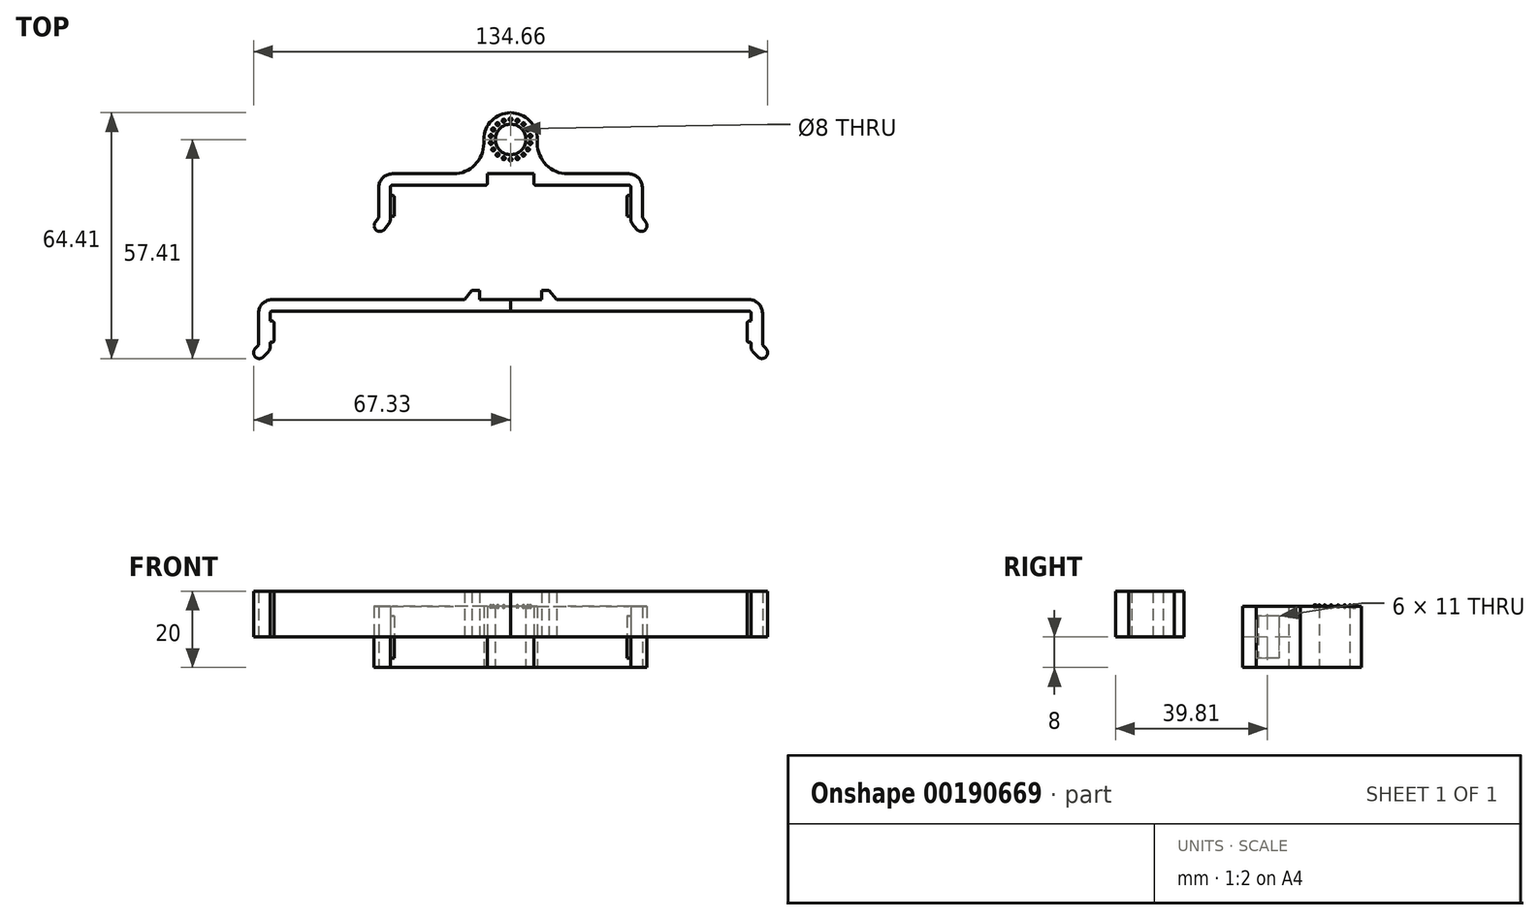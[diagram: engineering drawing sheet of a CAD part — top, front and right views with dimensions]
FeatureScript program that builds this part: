
annotation { "Feature Type Name" : "Feature", "Feature Type Description" : "" }
export const myFeature = defineFeature(function(context is Context, id is Id, definition is map)
    precondition{}
    {
        {
            var Q0;
            Q0=qCreatedBy(makeId("Top.planeOp"),FACE);
            var sketch = newSketch(context, id + "F0", { "sketchPlane" : qUnion([Q0])});
            skLineSegment(sketch, "E0", {"start": v(6.6, 0) * mm, "end": v(31, 0) * mm});
            skLineSegment(sketch, "E1", {"start": v(31.5, -0.5) * mm, "end": v(31.5, -2.6) * mm});
            skLineSegment(sketch, "E2.0", {"start": v(33.75, -2.6) * mm, "end": v(33.75, -2.6) * mm});
            skLineSegment(sketch, "E3.0", {"start": v(31, -8.1) * mm, "end": v(31, -8.1) * mm});
            skLineSegment(sketch, "E4.0", {"start": v(30.5, -3.1) * mm, "end": v(30.5, -8.1) * mm});
            skLineSegment(sketch, "E5.0", {"start": v(34.5, -0.5) * mm, "end": v(34.5, -8.55) * mm});
            skLineSegment(sketch, "E6.trimOffspring", {"start": v(31.5, -8.6) * mm, "end": v(31.5, -8.9) * mm});
            skPoint(sketch, "E7.visualSharp", {"position": v(31.5, 0) * mm});
            skArc(sketch, "E7.filletArc", {"start": v(31.5, -0.5) * mm, "mid": v(31.35, -0.15) * mm, "end": v(31, 0) * mm});
            skPoint(sketch, "E8.visualSharp", {"position": v(30.5, -8.1) * mm});
            skPoint(sketch, "E9.visualSharp", {"position": v(30.5, -2.6) * mm});
            skPoint(sketch, "E10.visualSharp", {"position": v(31.5, -8.1) * mm});
            skArc(sketch, "E10.filletArc", {"start": v(31.5, -8.6) * mm, "mid": v(31.35, -8.25) * mm, "end": v(31, -8.1) * mm});
            skPoint(sketch, "E11.visualSharp", {"position": v(31.5, -2.6) * mm});
            skPoint(sketch, "E12.visualSharp", {"position": v(34.5, 3) * mm});
            skArc(sketch, "E12.filletArc", {"start": v(34.5, -0.5) * mm, "mid": v(33.47, 1.97) * mm, "end": v(31, 3) * mm});
            skLineSegment(sketch, "E13", {"start": v(31, -2.6) * mm, "end": v(31.5, -2.6) * mm});
            skLineSegment(sketch, "E14", {"start": v(6.1, 3.1) * mm, "end": v(6.1, 0.5) * mm});
            skPoint(sketch, "E15.orphan", {"position": v(0, 0) * mm});
            skPoint(sketch, "E16.visualSharp", {"position": v(6.1, 0) * mm});
            skArc(sketch, "E16.filletArc", {"start": v(6.1, 0.5) * mm, "mid": v(6.25, 0.15) * mm, "end": v(6.6, 0) * mm});
            skPoint(sketch, "E17.visualSharp", {"position": v(9, 3) * mm});
            skLineSegment(sketch, "E18", {"start": v(0, 0) * mm, "end": v(0, 12) * mm, "construction": true});
            skArc(sketch, "E19", {"start": v(0, 8) * mm, "mid": v(4, 12) * mm, "end": v(0, 16) * mm});
            skLineSegment(sketch, "E20", {"start": v(0, 8) * mm, "end": v(0, 3) * mm});
            skLineSegment(sketch, "E21.0", {"start": v(33.25, -9.6) * mm, "end": v(34.5, -9.6) * mm, "construction": true});
            skLineSegment(sketch, "E22.0", {"start": v(33.25, -14.6) * mm, "end": v(35.5, -14.6) * mm, "construction": true});
            skLineSegment(sketch, "E23.0", {"start": v(35.5, -10.5) * mm, "end": v(35.5, -14.6) * mm, "construction": true});
            skLineSegment(sketch, "E24", {"start": v(31.94, -10.15) * mm, "end": v(33.06, -11.55) * mm});
            skLineSegment(sketch, "E25.0", {"start": v(34.5, -8.55) * mm, "end": v(35.4, -9.68) * mm});
            skLineSegment(sketch, "E26", {"start": v(31.5, -9.6) * mm, "end": v(33.84, -7.73) * mm, "construction": true});
            skLineSegment(sketch, "E27.0", {"start": v(35.17, -11.79) * mm, "end": v(35.17, -11.79) * mm});
            skPoint(sketch, "E28.visualSharp", {"position": v(34, -12.72) * mm});
            skArc(sketch, "E28.filletArc", {"start": v(33.06, -11.55) * mm, "mid": v(34.07, -12.1) * mm, "end": v(35.17, -11.79) * mm});
            skPoint(sketch, "E29.visualSharp", {"position": v(36.34, -10.85) * mm});
            skArc(sketch, "E29.filletArc", {"start": v(35.17, -11.79) * mm, "mid": v(35.72, -10.78) * mm, "end": v(35.4, -9.68) * mm});
            skPoint(sketch, "E30.visualSharp", {"position": v(31.5, -9.6) * mm});
            skArc(sketch, "E30.filletArc", {"start": v(31.5, -8.9) * mm, "mid": v(31.61, -9.56) * mm, "end": v(31.94, -10.15) * mm});
            skLineSegment(sketch, "E31.0", {"start": v(0, 3.1) * mm, "end": v(8.2, 3.1) * mm, "construction": true});
            skLineSegment(sketch, "E32", {"start": v(6.1, 3.1) * mm, "end": v(0, 3.1) * mm});
            skLineSegment(sketch, "E33.0", {"start": v(15, 3) * mm, "end": v(31, 3) * mm});
            skArc(sketch, "E34.0", {"start": v(7, 12) * mm, "mid": v(4.95, 16.95) * mm, "end": v(0, 19) * mm});
            skLineSegment(sketch, "E35.0", {"start": v(7, 0) * mm, "end": v(7, 12) * mm, "construction": true});
            skLineSegment(sketch, "E36", {"start": v(7, 11) * mm, "end": v(7, 12) * mm});
            skLineSegment(sketch, "E37", {"start": v(0, 19) * mm, "end": v(0, 16) * mm});
            skPoint(sketch, "E38.visualSharp", {"position": v(7, 3) * mm});
            skArc(sketch, "E38.filletArc", {"start": v(7, 11) * mm, "mid": v(9.34, 5.34) * mm, "end": v(15, 3) * mm});
            skLineSegment(sketch, "E39", {"start": v(30.5, -8.1) * mm, "end": v(31, -8.1) * mm});
            skArc(sketch, "E40.filletArc", {"start": v(31, -2.6) * mm, "mid": v(30.65, -2.75) * mm, "end": v(30.5, -3.1) * mm});
            skSolve(sketch);
        }
        {
            var Q0;
            Q0=makeQuery(id+"F0.imprint","IMPRINT",FACE,{"disambiguationData":[TD([[makeQuery(id+"F0.imprint","IMPRINT",EDGE,{"derivedFrom":sQuery(id+"F0.wireOp",EDGE,"E0")}),1.0]])]});
            extrude(context, id + "F1", {"entities" : qUnion([Q0]), "depth" : 5.5 * mm});
        }
        {
            var Q0;
            Q0=qCreatedBy(makeId("Top.planeOp"),FACE);
            cPlane(context, id + "F2", {"entities" : qUnion([Q0]), "cplaneType" : CPlaneType.OFFSET, "offset" : 8 * mm, "width" : 150 * mm, "height" : 150 * mm});
        }
        {
            var Q0;
            Q0=qCreatedBy(id+"F2.planeOp",FACE);
            var sketch = newSketch(context, id + "F3", { "sketchPlane" : qUnion([Q0])});
            skArc(sketch, "E41.0.0", {"start": v(6.1, 0.5) * mm, "mid": v(6.25, 0.15) * mm, "end": v(6.6, 0) * mm});
            skLineSegment(sketch, "E41.0.1", {"start": v(6.6, 0) * mm, "end": v(31, 0) * mm});
            skArc(sketch, "E41.0.2", {"start": v(31, 0) * mm, "mid": v(31.35, -0.15) * mm, "end": v(31.5, -0.5) * mm});
            skLineSegment(sketch, "E41.0.3", {"start": v(31.5, -0.5) * mm, "end": v(31.5, -8.6) * mm});
            skLineSegment(sketch, "E41.0.8", {"start": v(31.5, -8.6) * mm, "end": v(31.5, -8.9) * mm});
            skArc(sketch, "E41.0.9", {"start": v(31.5, -8.9) * mm, "mid": v(31.61, -9.56) * mm, "end": v(31.94, -10.15) * mm});
            skLineSegment(sketch, "E41.0.10", {"start": v(31.94, -10.15) * mm, "end": v(33.06, -11.55) * mm});
            skArc(sketch, "E41.0.11", {"start": v(33.06, -11.55) * mm, "mid": v(34.07, -12.1) * mm, "end": v(35.17, -11.79) * mm});
            skArc(sketch, "E41.0.12", {"start": v(35.17, -11.79) * mm, "mid": v(35.72, -10.78) * mm, "end": v(35.4, -9.68) * mm});
            skLineSegment(sketch, "E41.0.13", {"start": v(35.4, -9.68) * mm, "end": v(34.5, -8.55) * mm});
            skLineSegment(sketch, "E41.0.14", {"start": v(34.5, -8.55) * mm, "end": v(34.5, -0.5) * mm});
            skArc(sketch, "E41.0.15", {"start": v(34.5, -0.5) * mm, "mid": v(33.47, 1.97) * mm, "end": v(31, 3) * mm});
            skLineSegment(sketch, "E41.0.16", {"start": v(31, 3) * mm, "end": v(15, 3) * mm});
            skArc(sketch, "E41.0.17", {"start": v(15, 3) * mm, "mid": v(9.34, 5.34) * mm, "end": v(7, 11) * mm});
            skLineSegment(sketch, "E41.0.18", {"start": v(7, 11) * mm, "end": v(7, 12) * mm});
            skArc(sketch, "E41.0.19", {"start": v(7, 12) * mm, "mid": v(4.95, 16.95) * mm, "end": v(0, 19) * mm});
            skLineSegment(sketch, "E41.0.20", {"start": v(0, 19) * mm, "end": v(0, 16) * mm});
            skArc(sketch, "E41.0.21", {"start": v(0, 16) * mm, "mid": v(4, 12) * mm, "end": v(0, 8) * mm});
            skLineSegment(sketch, "E41.0.22", {"start": v(0, 8) * mm, "end": v(0, 3.1) * mm});
            skLineSegment(sketch, "E41.0.23", {"start": v(0, 3.1) * mm, "end": v(6.1, 3.1) * mm});
            skLineSegment(sketch, "E41.0.24", {"start": v(6.1, 3.1) * mm, "end": v(6.1, 0.5) * mm});
            skSolve(sketch);
        }
        {
            var Q0;
            Q0=qSketchRegion(id+"F3",true);
            extrude(context, id + "F4", {"entities" : qUnion([Q0]), "operationType" : NewBodyOperationType.ADD, "oppositeDirection" : true, "depth" : 2.5 * mm});
        }
        {
            var Q0;
            Q0=makeQuery(id+"F1.opExtrude","SWEPT_BODY",BODY,{"disambiguationData":[OSD([sQuery(id+"F0.wireOp",EDGE,"E0"),sQuery(id+"F0.wireOp",EDGE,"E1"),sQuery(id+"F0.wireOp",EDGE,"JgK67lIY-4EgY-ey94-oZCU-HRvDTyMh9sml"),sQuery(id+"F0.wireOp",EDGE,"E4.0"),sQuery(id+"F0.wireOp",EDGE,"94614247-38f6-4f2a-a7c6-92986ae7038c.0"),sQuery(id+"F0.wireOp",EDGE,"E5.0"),sQuery(id+"F0.wireOp",EDGE,"bafeba88-4bcf-4ffe-8af9-f0758a89d23e.0"),sQuery(id+"F0.wireOp",EDGE,"E6.trimOffspring"),sQuery(id+"F0.wireOp",EDGE,"E7.filletArc"),sQuery(id+"F0.wireOp",EDGE,"4b34f401-58b1-4bb0-b663-6c6aab183ffe.filletArc"),sQuery(id+"F0.wireOp",EDGE,"a385be46-2ddd-4659-8188-594981e60d19.filletArc"),sQuery(id+"F0.wireOp",EDGE,"dc32ce36-d1a5-4122-8cf5-4ddb1d333482.filletArc"),sQuery(id+"F0.wireOp",EDGE,"E8.filletArc"),sQuery(id+"F0.wireOp",EDGE,"E9.filletArc"),sQuery(id+"F0.wireOp",EDGE,"E10.filletArc"),sQuery(id+"F0.wireOp",EDGE,"E11.filletArc"),sQuery(id+"F0.wireOp",EDGE,"E12.filletArc"),sQuery(id+"F0.wireOp",EDGE,"RIqGV35R-ZyQh-7Wbn-B3qv-Q6Mvw9Py10aq")])]});
            var Q1;
            Q1=makeQuery(id+"F1.opExtrude","SWEPT_FACE",FACE,{"disambiguationData":[OSD([sQuery(id+"F0.wireOp",EDGE,"E20")])]});
            mirror(context, id + "F5", {"operationType" : NewBodyOperationType.ADD, "entities" : qUnion([Q0]), "mirrorPlane" : qUnion([Q1])});
        }
        {
            var Q0;
            Q0=makeQuery(id+"F1.opExtrude","SWEPT_BODY",BODY,{"disambiguationData":[OSD([sQuery(id+"F0.wireOp",EDGE,"E0"),sQuery(id+"F0.wireOp",EDGE,"E1"),sQuery(id+"F0.wireOp",EDGE,"E4.0"),sQuery(id+"F0.wireOp",EDGE,"E5.0"),sQuery(id+"F0.wireOp",EDGE,"E6.trimOffspring"),sQuery(id+"F0.wireOp",EDGE,"E7.filletArc"),sQuery(id+"F0.wireOp",EDGE,"E8.filletArc"),sQuery(id+"F0.wireOp",EDGE,"E10.filletArc"),sQuery(id+"F0.wireOp",EDGE,"E12.filletArc"),sQuery(id+"F0.wireOp",EDGE,"E13"),sQuery(id+"F0.wireOp",EDGE,"E14"),sQuery(id+"F0.wireOp",EDGE,"E16.filletArc"),sQuery(id+"F0.wireOp",EDGE,"E19"),sQuery(id+"F0.wireOp",EDGE,"E20"),sQuery(id+"F0.wireOp",EDGE,"E24"),sQuery(id+"F0.wireOp",EDGE,"E25.0"),sQuery(id+"F0.wireOp",EDGE,"E28.filletArc"),sQuery(id+"F0.wireOp",EDGE,"E29.filletArc"),sQuery(id+"F0.wireOp",EDGE,"E30.filletArc"),sQuery(id+"F0.wireOp",EDGE,"E32"),sQuery(id+"F0.wireOp",EDGE,"E33.0"),sQuery(id+"F0.wireOp",EDGE,"E34.0"),sQuery(id+"F0.wireOp",EDGE,"E36"),sQuery(id+"F0.wireOp",EDGE,"E37"),sQuery(id+"F0.wireOp",EDGE,"E38.filletArc")])]});
            var Q1;
            Q1=qCreatedBy(makeId("Top.planeOp"),FACE);
            mirror(context, id + "F6", {"operationType" : NewBodyOperationType.ADD, "entities" : qUnion([Q0]), "mirrorPlane" : qUnion([Q1])});
        }
        {
            var Q0;
            Q0=qCreatedBy(makeId("Top.planeOp"),FACE);
            var sketch = newSketch(context, id + "F7", { "sketchPlane" : qUnion([Q0])});
            skLineSegment(sketch, "E42", {"start": v(0, 0) * mm, "end": v(0, -30) * mm, "construction": true});
            skLineSegment(sketch, "E43", {"start": v(0, -30) * mm, "end": v(8.1, -30) * mm});
            skLineSegment(sketch, "E44", {"start": v(8.1, -30) * mm, "end": v(8.1, -27.5) * mm});
            skLineSegment(sketch, "E45", {"start": v(0, -30) * mm, "end": v(0, -33) * mm});
            skLineSegment(sketch, "E46", {"start": v(0, -33) * mm, "end": v(62.5, -33) * mm});
            skLineSegment(sketch, "E47", {"start": v(63, -33.5) * mm, "end": v(63, -35.5) * mm});
            skLineSegment(sketch, "E48", {"start": v(62.5, -30) * mm, "end": v(12.1, -30) * mm});
            skLineSegment(sketch, "E49", {"start": v(62.9, -35.6) * mm, "end": v(62.5, -35.6) * mm});
            skPoint(sketch, "E50.visualSharp", {"position": v(63, -33) * mm});
            skArc(sketch, "E50.filletArc", {"start": v(63, -33.5) * mm, "mid": v(62.85, -33.15) * mm, "end": v(62.5, -33) * mm});
            skPoint(sketch, "E51.visualSharp", {"position": v(63, -35.6) * mm});
            skPoint(sketch, "E52.visualSharp", {"position": v(69, -30) * mm});
            skLineSegment(sketch, "E53", {"start": v(8.1, -27.5) * mm, "end": v(10.1, -27.5) * mm});
            skLineSegment(sketch, "E54.0", {"start": v(62, -36.1) * mm, "end": v(62, -40.7) * mm});
            skLineSegment(sketch, "E55.0", {"start": v(62.9, -41.2) * mm, "end": v(62.5, -41.2) * mm});
            skLineSegment(sketch, "E56.0", {"start": v(63, -43.2) * mm, "end": v(60, -43.2) * mm, "construction": true});
            skArc(sketch, "E57.filletArc", {"start": v(62.9, -35.6) * mm, "mid": v(62.97, -35.57) * mm, "end": v(63, -35.5) * mm});
            skPoint(sketch, "E58.visualSharp", {"position": v(63, -41.2) * mm});
            skPoint(sketch, "E59.visualSharp", {"position": v(62, -35.6) * mm});
            skArc(sketch, "E59.filletArc", {"start": v(62.5, -35.6) * mm, "mid": v(62.15, -35.75) * mm, "end": v(62, -36.1) * mm});
            skPoint(sketch, "E60.visualSharp", {"position": v(62, -41.2) * mm});
            skArc(sketch, "E60.filletArc", {"start": v(62, -40.7) * mm, "mid": v(62.15, -41.05) * mm, "end": v(62.5, -41.2) * mm});
            skLineSegment(sketch, "E61.0", {"start": v(66, -47.2) * mm, "end": v(59.97, -47.2) * mm, "construction": true});
            skLineSegment(sketch, "E62.0", {"start": v(66, -33.5) * mm, "end": v(66, -41.96) * mm});
            skPoint(sketch, "E63.visualSharp", {"position": v(66, -30) * mm});
            skArc(sketch, "E63.filletArc", {"start": v(66, -33.5) * mm, "mid": v(64.97, -31.03) * mm, "end": v(62.5, -30) * mm});
            skLineSegment(sketch, "E64.trimOffspring", {"start": v(63, -41.3) * mm, "end": v(63, -42.37) * mm});
            skPoint(sketch, "E65.visualSharp", {"position": v(63, -47.2) * mm});
            skPoint(sketch, "E66.visualSharp", {"position": v(66, -47.2) * mm});
            skLineSegment(sketch, "E67.0", {"start": v(67, -51.3) * mm, "end": v(67, -58.78) * mm, "construction": true});
            skLineSegment(sketch, "E68", {"start": v(63.59, -43.79) * mm, "end": v(64.77, -44.97) * mm});
            skPoint(sketch, "E68.endSnap0", {"position": v(67, -55.04) * mm});
            skLineSegment(sketch, "E69.0", {"start": v(66, -41.96) * mm, "end": v(66.89, -42.85) * mm});
            skLineSegment(sketch, "E70", {"start": v(63, -43.2) * mm, "end": v(65.12, -41.08) * mm, "construction": true});
            skLineSegment(sketch, "E71.0", {"start": v(66.89, -44.97) * mm, "end": v(66.89, -44.97) * mm});
            skPoint(sketch, "E72.orphan", {"position": v(67, -47.2) * mm});
            skArc(sketch, "E73.filletArc", {"start": v(63, -41.3) * mm, "mid": v(62.97, -41.23) * mm, "end": v(62.9, -41.2) * mm});
            skPoint(sketch, "E74.visualSharp", {"position": v(63, -43.2) * mm});
            skArc(sketch, "E74.filletArc", {"start": v(63, -42.37) * mm, "mid": v(63.15, -43.14) * mm, "end": v(63.59, -43.79) * mm});
            skPoint(sketch, "E75.visualSharp", {"position": v(65.83, -46.03) * mm});
            skArc(sketch, "E75.filletArc", {"start": v(64.77, -44.97) * mm, "mid": v(65.83, -45.4) * mm, "end": v(66.89, -44.97) * mm});
            skPoint(sketch, "E76.visualSharp", {"position": v(67.95, -43.9) * mm});
            skArc(sketch, "E76.filletArc", {"start": v(66.89, -44.97) * mm, "mid": v(67.33, -43.9) * mm, "end": v(66.89, -42.85) * mm});
            skLineSegment(sketch, "E77.0", {"start": v(12.1, -30) * mm, "end": v(12.1, -27.5) * mm, "construction": true});
            skLineSegment(sketch, "E78", {"start": v(10.1, -27.5) * mm, "end": v(12.1, -30) * mm});
            skSolve(sketch);
        }
        {
            var Q0;
            Q0=makeQuery(id+"F7.imprint","IMPRINT",FACE,{"disambiguationData":[TD([[makeQuery(id+"F7.imprint","IMPRINT",EDGE,{"derivedFrom":sQuery(id+"F7.wireOp",EDGE,"E43")}),-1.0]])]});
            extrude(context, id + "F8", {"entities" : qUnion([Q0]), "depth" : 12 * mm});
        }
        {
            var Q0;
            Q0=makeQuery(id+"F8.opExtrude","SWEPT_BODY",BODY,{"disambiguationData":[OSD([sQuery(id+"F7.wireOp",EDGE,"E43"),sQuery(id+"F7.wireOp",EDGE,"E44"),sQuery(id+"F7.wireOp",EDGE,"E45"),sQuery(id+"F7.wireOp",EDGE,"E46"),sQuery(id+"F7.wireOp",EDGE,"E47"),sQuery(id+"F7.wireOp",EDGE,"E48"),sQuery(id+"F7.wireOp",EDGE,"E49"),sQuery(id+"F7.wireOp",EDGE,"K0LTJFh5-bBiZ-CepU-s1b6-8ufsYFky9yuO"),sQuery(id+"F7.wireOp",EDGE,"o9zvkVCV-yeKc-U0ps-SUTC-iAieyRe5ZOSn"),sQuery(id+"F7.wireOp",EDGE,"E50.filletArc"),sQuery(id+"F7.wireOp",EDGE,"E51.filletArc"),sQuery(id+"F7.wireOp",EDGE,"9fb69594-6c0b-451a-b786-1d248d921512.filletArc"),sQuery(id+"F7.wireOp",EDGE,"cec750f1-cf65-49dd-8b05-a30b1d44f730.filletArc"),sQuery(id+"F7.wireOp",EDGE,"E52.filletArc"),sQuery(id+"F7.wireOp",EDGE,"7ef73556-ab24-4602-92b6-dd3b93125750.filletArc"),sQuery(id+"F7.wireOp",EDGE,"E53"),sQuery(id+"F7.wireOp",EDGE,"mFBaEJeU-63ch-cngc-R38N-QltwovzmawJg")])]});
            var Q1;
            Q1=makeQuery(id+"F8.opExtrude","SWEPT_FACE",FACE,{"disambiguationData":[OSD([sQuery(id+"F7.wireOp",EDGE,"E45")])]});
            mirror(context, id + "F9", {"operationType" : NewBodyOperationType.ADD, "entities" : qUnion([Q0]), "mirrorPlane" : qUnion([Q1])});
        }
        {
            var Q0;
            {var subQ0=makeQuery(id+"F4.opExtrude","CAP_FACE",FACE,{"disambiguationData":[OSD([sQuery(id+"F3.wireOp",EDGE,"E41.0.0"),sQuery(id+"F3.wireOp",EDGE,"E41.0.1"),sQuery(id+"F3.wireOp",EDGE,"E41.0.2"),sQuery(id+"F3.wireOp",EDGE,"E41.0.3"),sQuery(id+"F3.wireOp",EDGE,"E41.0.8"),sQuery(id+"F3.wireOp",EDGE,"E41.0.9"),sQuery(id+"F3.wireOp",EDGE,"E41.0.10"),sQuery(id+"F3.wireOp",EDGE,"E41.0.11"),sQuery(id+"F3.wireOp",EDGE,"E41.0.12"),sQuery(id+"F3.wireOp",EDGE,"E41.0.13"),sQuery(id+"F3.wireOp",EDGE,"E41.0.14"),sQuery(id+"F3.wireOp",EDGE,"E41.0.15"),sQuery(id+"F3.wireOp",EDGE,"E41.0.16"),sQuery(id+"F3.wireOp",EDGE,"E41.0.17"),sQuery(id+"F3.wireOp",EDGE,"E41.0.18"),sQuery(id+"F3.wireOp",EDGE,"E41.0.19"),sQuery(id+"F3.wireOp",EDGE,"E41.0.20"),sQuery(id+"F3.wireOp",EDGE,"E41.0.21"),sQuery(id+"F3.wireOp",EDGE,"E41.0.22"),sQuery(id+"F3.wireOp",EDGE,"E41.0.23"),sQuery(id+"F3.wireOp",EDGE,"E41.0.24")])],"isStart":true});Q0=makeQuery(id+"F5.boolean.opBoolean","MERGE",FACE,{"derivedFrom":[subQ0,makeQuery(id+"F5.opPattern","COPY",FACE,{"derivedFrom":subQ0,"instanceName":"1"})]});}
            var sketch = newSketch(context, id + "F10", { "sketchPlane" : qUnion([Q0])});
            skCircle(sketch, "E79", {"center": v(0, 12) * mm, "radius": 5.25 * mm, "construction": true});
            skLineSegment(sketch, "E80", {"start": v(0, 12) * mm, "end": v(0, 20.76) * mm, "construction": true});
            skPoint(sketch, "E80.endSnap0", {"position": v(0, 19) * mm});
            skCircle(sketch, "E81", {"center": v(0, 17.25) * mm, "radius": 0.4 * mm});
            skLineSegment(sketch, "E82", {"start": v(0, 12) * mm, "end": v(0, 2.14) * mm, "construction": true});
            skPoint(sketch, "E82.endSnap0", {"position": v(0, 3.1) * mm});
            skLineSegment(sketch, "E83", {"start": v(0, 17.65) * mm, "end": v(0, 16.85) * mm});
            skSolve(sketch);
        }
        {
            var Q0;
            {var subQ0=sQuery(id+"F10.wireOp",EDGE,"E83");Q0=makeQuery(id+"F10.imprint","IMPRINT",FACE,{"disambiguationData":[TD([[makeQuery(id+"F10.imprint","IMPRINT",EDGE,{"derivedFrom":subQ0}),-1.0]])]});}
            var Q1;
            Q1=sQuery(id+"F10.wireOp",EDGE,"E80");
            revolve(context, id + "F11", {"entities" : qUnion([Q0]), "axis" : qUnion([Q1]), "revolveType" : RevolveType.FULL});
        }
        {
            var Q0;
            Q0=makeQuery(id+"F11.opRevolve","SWEPT_BODY",BODY,{"disambiguationData":[OSD([sQuery(id+"F10.wireOp",EDGE,"E81"),sQuery(id+"F10.wireOp",EDGE,"E83")])]});
            var Q1;
            {var subQ0=makeQuery(id+"F4.boolean.opBoolean","MERGE",FACE,{"derivedFrom":[makeQuery(id+"F1.opExtrude","SWEPT_FACE",FACE,{"disambiguationData":[OSD([sQuery(id+"F0.wireOp",EDGE,"E19")])]}),makeQuery(id+"F4.opExtrude","SWEPT_FACE",FACE,{"disambiguationData":[OSD([sQuery(id+"F3.wireOp",EDGE,"E41.0.21")])]})]});var subQ1=makeQuery(id+"F5.boolean.opBoolean","MERGE",FACE,{"derivedFrom":[subQ0,makeQuery(id+"F5.opPattern","COPY",FACE,{"derivedFrom":subQ0,"instanceName":"1"})]});Q1=makeQuery(id+"F6.boolean.opBoolean","MERGE",FACE,{"derivedFrom":[subQ1,makeQuery(id+"F6.opPattern","COPY",FACE,{"derivedFrom":subQ1,"instanceName":"1"})]});}
            circularPattern(context, id + "F12", {"entities" : qUnion([Q0]), "axis" : qUnion([Q1]), "angle" : 360 * degree, "instanceCount" : 18, "equalSpace" : true});
        }
    });
